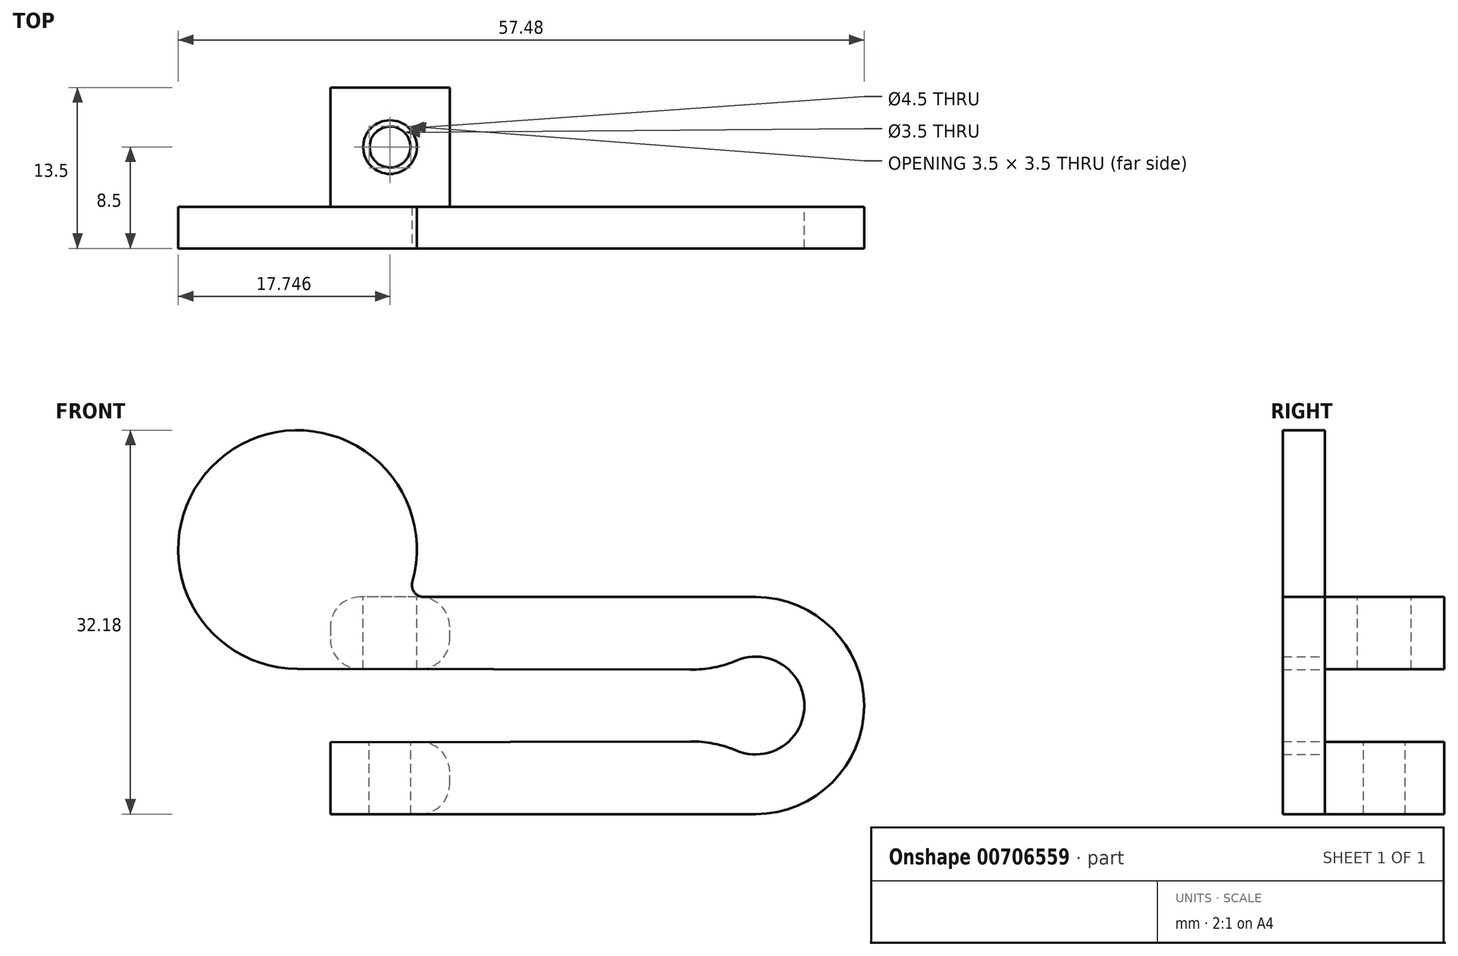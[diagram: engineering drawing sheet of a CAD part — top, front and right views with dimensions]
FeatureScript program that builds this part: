
annotation { "Feature Type Name" : "Feature", "Feature Type Description" : "" }
export const myFeature = defineFeature(function(context is Context, id is Id, definition is map)
    precondition{}
    {
        {
            var Q0;
            Q0=qCreatedBy(makeId("Front.planeOp"),FACE);
            var sketch = newSketch(context, id + "F0", { "sketchPlane" : qUnion([Q0])});
            skArc(sketch, "E0", {"start": v(-2.8, -3) * mm, "mid": v(4.1, 0) * mm, "end": v(-2.8, 3) * mm});
            skArc(sketch, "E1", {"start": v(0, -9.1) * mm, "mid": v(9.1, 0) * mm, "end": v(0, 9.1) * mm});
            skLineSegment(sketch, "E2", {"start": v(0, 9.1) * mm, "end": v(-45, 9.1) * mm});
            skLineSegment(sketch, "E3", {"start": v(0, -9.1) * mm, "end": v(-45, -9.1) * mm});
            skLineSegment(sketch, "E4", {"start": v(-45, 9.1) * mm, "end": v(-45, 3.1) * mm});
            skLineSegment(sketch, "E5", {"start": v(-45, -3.1) * mm, "end": v(-45, -9.1) * mm});
            skLineSegment(sketch, "E6", {"start": v(-45, 3.1) * mm, "end": v(-2.8, 3) * mm});
            skLineSegment(sketch, "E7", {"start": v(-45, -3.1) * mm, "end": v(-2.8, -3) * mm});
            skSolve(sketch);
        }
        {
            var Q0;
            Q0 = qSketchRegion(id + "F0", true);
            extrude(context, id + "F1", {"entities" : qUnion([Q0]), "depth" : 3.5 * mm, "offsetDistance" : 25 * mm});
        }
        {
            var Q0;
            Q0=makeQuery(id+"F1.opExtrude","CAP_FACE",FACE,{"disambiguationData":[OSD([sQuery(id+"F0.wireOp",EDGE,"E0"),sQuery(id+"F0.wireOp",EDGE,"E1"),sQuery(id+"F0.wireOp",EDGE,"E2"),sQuery(id+"F0.wireOp",EDGE,"E3"),sQuery(id+"F0.wireOp",EDGE,"E4"),sQuery(id+"F0.wireOp",EDGE,"E5"),sQuery(id+"F0.wireOp",EDGE,"E6"),sQuery(id+"F0.wireOp",EDGE,"E7")])],"isStart":true});
            var sketch = newSketch(context, id + "F2", { "sketchPlane" : qUnion([Q0])});
            skLineSegment(sketch, "E8", {"start": v(25.63, 9.1) * mm, "end": v(35.63, 9.1) * mm});
            skLineSegment(sketch, "E9", {"start": v(35.63, 9.1) * mm, "end": v(35.63, 3.08) * mm});
            skLineSegment(sketch, "E10", {"start": v(35.63, 3.08) * mm, "end": v(25.63, 3.05) * mm});
            skLineSegment(sketch, "E11", {"start": v(25.63, 3.05) * mm, "end": v(25.63, 9.1) * mm});
            skLineSegment(sketch, "E12", {"start": v(35.63, -3.08) * mm, "end": v(35.63, -9.1) * mm});
            skLineSegment(sketch, "E13", {"start": v(35.63, -9.1) * mm, "end": v(25.63, -9.1) * mm});
            skLineSegment(sketch, "E14", {"start": v(25.63, -9.1) * mm, "end": v(25.63, -3.05) * mm});
            skLineSegment(sketch, "E15", {"start": v(25.63, -3.05) * mm, "end": v(35.63, -3.08) * mm});
            skSolve(sketch);
        }
        {
            var Q0;
            Q0 = qSketchRegion(id + "F2", true);
            extrude(context, id + "F3", {"entities" : qUnion([Q0]), "operationType" : NewBodyOperationType.ADD, "depth" : 10 * mm, "offsetDistance" : 25 * mm});
        }
        {
            var Q0;
            Q0=makeQuery(id+"F3.boolean.opBoolean","MERGE",FACE,{"derivedFrom":[makeQuery(id+"F1.opExtrude","SWEPT_FACE",FACE,{"disambiguationData":[OSD([sQuery(id+"F0.wireOp",EDGE,"E2")])]}),makeQuery(id+"F3.opExtrude","SWEPT_FACE",FACE,{"disambiguationData":[OSD([sQuery(id+"F2.wireOp",EDGE,"pMjsHXQ3-Vv6g-jYmR-rTr3-SYkMuq2vQOZm")])]})]});
            var sketch = newSketch(context, id + "F4", { "sketchPlane" : qUnion([Q0])});
            skCircle(sketch, "E16", {"center": v(-30.63, 5) * mm, "radius": 2.25 * mm});
            skSolve(sketch);
        }
        {
            var Q0;
            Q0 = qSketchRegion(id + "F4", true);
            extrude(context, id + "F5", {"entities" : qUnion([Q0]), "operationType" : NewBodyOperationType.REMOVE, "oppositeDirection" : true, "depth" : 10 * mm, "offsetDistance" : 25 * mm});
        }
        {
            var Q0;
            Q0=makeQuery(id+"F3.boolean.opBoolean","MERGE",FACE,{"derivedFrom":[makeQuery(id+"F1.opExtrude","SWEPT_FACE",FACE,{"disambiguationData":[OSD([sQuery(id+"F0.wireOp",EDGE,"E2")])]}),makeQuery(id+"F3.opExtrude","SWEPT_FACE",FACE,{"disambiguationData":[OSD([sQuery(id+"F2.wireOp",EDGE,"pMjsHXQ3-Vv6g-jYmR-rTr3-SYkMuq2vQOZm")])]})]});
            var sketch = newSketch(context, id + "F6", { "sketchPlane" : qUnion([Q0])});
            skCircle(sketch, "E17", {"center": v(-30.63, 5) * mm, "radius": 1.75 * mm});
            skSolve(sketch);
        }
        {
            var Q0;
            Q0 = qSketchRegion(id + "F6", true);
            extrude(context, id + "F7", {"entities" : qUnion([Q0]), "operationType" : NewBodyOperationType.REMOVE, "oppositeDirection" : true, "depth" : 25 * mm, "offsetDistance" : 25 * mm});
        }
        {
            var Q0;
            Q0=makeQuery(id+"F1.opExtrude","CAP_FACE",FACE,{"disambiguationData":[OSD([sQuery(id+"F0.wireOp",EDGE,"E0"),sQuery(id+"F0.wireOp",EDGE,"E1"),sQuery(id+"F0.wireOp",EDGE,"E2"),sQuery(id+"F0.wireOp",EDGE,"E3"),sQuery(id+"F0.wireOp",EDGE,"E4"),sQuery(id+"F0.wireOp",EDGE,"E5"),sQuery(id+"F0.wireOp",EDGE,"E6"),sQuery(id+"F0.wireOp",EDGE,"E7")])],"isStart":false});
            var sketch = newSketch(context, id + "F8", { "sketchPlane" : qUnion([Q0])});
            skCircle(sketch, "E18", {"center": v(-38.38, 13.08) * mm, "radius": 10 * mm});
            skSolve(sketch);
        }
        {
            var Q0;
            Q0 = qSketchRegion(id + "F8", true);
            var Q1;
            Q1=makeQuery(id+"F1.opExtrude","CAP_FACE",FACE,{"disambiguationData":[OSD([sQuery(id+"F0.wireOp",EDGE,"E0"),sQuery(id+"F0.wireOp",EDGE,"E1"),sQuery(id+"F0.wireOp",EDGE,"E2"),sQuery(id+"F0.wireOp",EDGE,"E3"),sQuery(id+"F0.wireOp",EDGE,"E4"),sQuery(id+"F0.wireOp",EDGE,"E5"),sQuery(id+"F0.wireOp",EDGE,"E6"),sQuery(id+"F0.wireOp",EDGE,"E7")])],"isStart":true});
            extrude(context, id + "F9", {"entities" : qUnion([Q0]), "operationType" : NewBodyOperationType.ADD, "endBound" : BoundingType.UP_TO_SURFACE, "oppositeDirection" : true, "depth" : 25 * mm, "endBoundEntityFace" : qUnion([Q1]), "offsetDistance" : 25 * mm});
        }
        {
            var Q0;
            Q0=makeQuery(id+"F3.boolean.opBoolean","MERGE",EDGE,{"derivedFrom":[makeQuery(id+"F1.opExtrude","SWEPT_EDGE",EDGE,{"disambiguationData":[OSD([sQuery(id+"F0.wireOp",EDGE,"E4"),sQuery(id+"F0.wireOp",EDGE,"E6")])]}),makeQuery(id+"F3.opExtrude","SWEPT_EDGE",EDGE,{"disambiguationData":[OSD([sQuery(id+"F2.wireOp",EDGE,"VnQjhJev-6pRI-Fd25-12oq-4aVABt8pIq3j"),sQuery(id+"F2.wireOp",EDGE,"sn0lMUrj-LP6i-RNEb-L6wM-ymogfDIRcxsj")])]})]});
            var Q1;
            Q1=makeQuery(id+"F3.boolean.opBoolean","MERGE",EDGE,{"derivedFrom":[makeQuery(id+"F1.opExtrude","SWEPT_EDGE",EDGE,{"disambiguationData":[OSD([sQuery(id+"F0.wireOp",EDGE,"E2"),sQuery(id+"F0.wireOp",EDGE,"E4")])]}),makeQuery(id+"F3.opExtrude","SWEPT_EDGE",EDGE,{"disambiguationData":[OSD([sQuery(id+"F2.wireOp",EDGE,"pMjsHXQ3-Vv6g-jYmR-rTr3-SYkMuq2vQOZm"),sQuery(id+"F2.wireOp",EDGE,"VnQjhJev-6pRI-Fd25-12oq-4aVABt8pIq3j")])]})]});
            fillet(context, id + "F10", {"entities" : qUnion([Q0, Q1]), "radius" : 3 * mm, "tangentPropagation" : true, "allowEdgeOverflow" : false});
        }
        {
            var Q0;
            Q0=makeQuery(id+"F1.opExtrude","SWEPT_EDGE",EDGE,{"disambiguationData":[OSD([sQuery(id+"F0.wireOp",EDGE,"E0"),sQuery(id+"F0.wireOp",EDGE,"E7")])]});
            var Q1;
            Q1=makeQuery(id+"F1.opExtrude","SWEPT_EDGE",EDGE,{"disambiguationData":[OSD([sQuery(id+"F0.wireOp",EDGE,"E0"),sQuery(id+"F0.wireOp",EDGE,"E6")])]});
            fillet(context, id + "F11", {"entities" : qUnion([Q0, Q1]), "radius" : 10 * mm, "tangentPropagation" : true, "allowEdgeOverflow" : false});
        }
        {
            var Q0;
            Q0=makeQuery(id+"F10.opFillet","BLEND_EDGE",EDGE,{"blendedFrom":[makeQuery(id+"F1.opExtrude","SWEPT_EDGE",EDGE,{"disambiguationData":[OSD([sQuery(id+"F0.wireOp",EDGE,"E4"),sQuery(id+"F0.wireOp",EDGE,"E6")])]}),makeQuery(id+"F9.opExtrude","SWEPT_FACE",FACE,{"disambiguationData":[OSD([sQuery(id+"F8.wireOp",EDGE,"E18")])]})],"blendedInto":[makeQuery(id+"F9.opExtrude","SWEPT_FACE",FACE,{"disambiguationData":[OSD([sQuery(id+"F8.wireOp",EDGE,"E18")])]})]});
            fillet(context, id + "F12", {"entities" : qUnion([Q0]), "radius" : 5 * mm, "tangentPropagation" : true, "allowEdgeOverflow" : false});
        }
        {
            var Q0;
            Q0=makeQuery(id+"F9.boolean.opBoolean","INTERSECT",EDGE,{"derivedFrom":[makeQuery(id+"F3.boolean.opBoolean","MERGE",FACE,{"derivedFrom":[makeQuery(id+"F1.opExtrude","SWEPT_FACE",FACE,{"disambiguationData":[OSD([sQuery(id+"F0.wireOp",EDGE,"E2")])]}),makeQuery(id+"F3.opExtrude","SWEPT_FACE",FACE,{"disambiguationData":[OSD([sQuery(id+"F2.wireOp",EDGE,"E8")])]})]}),makeQuery(id+"F9.opExtrude","SWEPT_FACE",FACE,{"disambiguationData":[OSD([sQuery(id+"F8.wireOp",EDGE,"E18")])]})]});
            fillet(context, id + "F13", {"entities" : qUnion([Q0]), "radius" : 1 * mm, "tangentPropagation" : true, "allowEdgeOverflow" : false});
        }
        {
            var Q0;
            {var subQ0=sQuery(id+"F0.wireOp",EDGE,"E5");var subQ1=sQuery(id+"F0.wireOp",EDGE,"E7");var subQ2=sQuery(id+"F0.wireOp",EDGE,"E3");Q0=makeQuery(id+"F3.boolean.opBoolean","SPLIT",FACE,{"disambiguationData":[TD([makeQuery(id+"F1.opExtrude","SWEPT_FACE",FACE,{"disambiguationData":[OSD([subQ0])]})])],"derivedFrom":makeQuery(id+"F1.opExtrude","CAP_FACE",FACE,{"disambiguationData":[OSD([sQuery(id+"F0.wireOp",EDGE,"E0"),sQuery(id+"F0.wireOp",EDGE,"E1"),sQuery(id+"F0.wireOp",EDGE,"E2"),subQ2,sQuery(id+"F0.wireOp",EDGE,"E4"),subQ0,sQuery(id+"F0.wireOp",EDGE,"E6"),subQ1])],"isStart":true})});}
            var sketch = newSketch(context, id + "F14", { "sketchPlane" : qUnion([Q0])});
            skLineSegment(sketch, "E19", {"start": v(35.63, -3.08) * mm, "end": v(45, -3.1) * mm});
            skLineSegment(sketch, "E20", {"start": v(45, -3.1) * mm, "end": v(45, -9.1) * mm});
            skLineSegment(sketch, "E21", {"start": v(45, -9.1) * mm, "end": v(35.63, -9.1) * mm});
            skLineSegment(sketch, "E22", {"start": v(35.63, -9.1) * mm, "end": v(35.63, -3.08) * mm});
            skSolve(sketch);
        }
        {
            var Q0;
            Q0 = qSketchRegion(id + "F14", true);
            extrude(context, id + "F15", {"entities" : qUnion([Q0]), "operationType" : NewBodyOperationType.REMOVE, "oppositeDirection" : true, "depth" : 25 * mm, "offsetDistance" : 25 * mm});
        }
        {
            var Q0;
            Q0=makeQuery(id+"F15.boolean.opBoolean","MERGE",EDGE,{"derivedFrom":[makeQuery(id+"F3.opExtrude","SWEPT_EDGE",EDGE,{"disambiguationData":[OSD([sQuery(id+"F0.wireOp",EDGE,"E7"),sQuery(id+"F2.wireOp",EDGE,"E12"),sQuery(id+"F2.wireOp",EDGE,"E15")])]}),makeQuery(id+"F15.opExtrude","SWEPT_EDGE",EDGE,{"disambiguationData":[OSD([sQuery(id+"F14.wireOp",EDGE,"E19"),sQuery(id+"F14.wireOp",EDGE,"E22")])]})]});
            var Q1;
            Q1=makeQuery(id+"F15.boolean.opBoolean","MERGE",EDGE,{"derivedFrom":[makeQuery(id+"F3.opExtrude","SWEPT_EDGE",EDGE,{"disambiguationData":[OSD([sQuery(id+"F0.wireOp",EDGE,"E3"),sQuery(id+"F2.wireOp",EDGE,"E12"),sQuery(id+"F2.wireOp",EDGE,"E13")])]}),makeQuery(id+"F15.opExtrude","SWEPT_EDGE",EDGE,{"disambiguationData":[OSD([sQuery(id+"F14.wireOp",EDGE,"E21"),sQuery(id+"F14.wireOp",EDGE,"E22")])]})]});
            var Q2;
            Q2=makeQuery(id+"F3.opExtrude","SWEPT_EDGE",EDGE,{"disambiguationData":[OSD([sQuery(id+"F0.wireOp",EDGE,"E7"),sQuery(id+"F2.wireOp",EDGE,"E14"),sQuery(id+"F2.wireOp",EDGE,"E15")])]});
            var Q3;
            Q3=makeQuery(id+"F3.opExtrude","SWEPT_EDGE",EDGE,{"disambiguationData":[OSD([sQuery(id+"F0.wireOp",EDGE,"E3"),sQuery(id+"F2.wireOp",EDGE,"E13"),sQuery(id+"F2.wireOp",EDGE,"E14")])]});
            var Q4;
            Q4=makeQuery(id+"F3.opExtrude","SWEPT_EDGE",EDGE,{"disambiguationData":[OSD([sQuery(id+"F0.wireOp",EDGE,"E2"),sQuery(id+"F2.wireOp",EDGE,"E8"),sQuery(id+"F2.wireOp",EDGE,"E11")])]});
            var Q5;
            Q5=makeQuery(id+"F3.opExtrude","SWEPT_EDGE",EDGE,{"disambiguationData":[OSD([sQuery(id+"F0.wireOp",EDGE,"E6"),sQuery(id+"F2.wireOp",EDGE,"E10"),sQuery(id+"F2.wireOp",EDGE,"E11")])]});
            var Q6;
            Q6=makeQuery(id+"F13.opFillet","BLEND_EDGE",EDGE,{"blendedFrom":[makeQuery(id+"F9.boolean.opBoolean","INTERSECT",EDGE,{"derivedFrom":[makeQuery(id+"F3.boolean.opBoolean","MERGE",FACE,{"derivedFrom":[makeQuery(id+"F1.opExtrude","SWEPT_FACE",FACE,{"disambiguationData":[OSD([sQuery(id+"F0.wireOp",EDGE,"E2")])]}),makeQuery(id+"F3.opExtrude","SWEPT_FACE",FACE,{"disambiguationData":[OSD([sQuery(id+"F2.wireOp",EDGE,"E8")])]})]}),makeQuery(id+"F9.opExtrude","SWEPT_FACE",FACE,{"disambiguationData":[OSD([sQuery(id+"F8.wireOp",EDGE,"E18")])]})]}),makeQuery(id+"F3.opExtrude","SWEPT_FACE",FACE,{"disambiguationData":[OSD([sQuery(id+"F2.wireOp",EDGE,"E9")])]})],"blendedInto":[makeQuery(id+"F3.opExtrude","SWEPT_FACE",FACE,{"disambiguationData":[OSD([sQuery(id+"F2.wireOp",EDGE,"E9")])]})]});
            var Q7;
            Q7=makeQuery(id+"F3.opExtrude","SWEPT_EDGE",EDGE,{"disambiguationData":[OSD([sQuery(id+"F0.wireOp",EDGE,"E6"),sQuery(id+"F2.wireOp",EDGE,"E9"),sQuery(id+"F2.wireOp",EDGE,"E10")])]});
            fillet(context, id + "F16", {"entities" : qUnion([Q0, Q1, Q2, Q3, Q4, Q5, Q6, Q7]), "radius" : 2.5 * mm, "tangentPropagation" : true, "allowEdgeOverflow" : false});
        }
        {
            var Q0;
            Q0=makeQuery(id+"F3.opExtrude","SWEPT_EDGE",EDGE,{"disambiguationData":[OSD([sQuery(id+"F0.wireOp",EDGE,"E2"),sQuery(id+"F2.wireOp",EDGE,"E8"),sQuery(id+"F2.wireOp",EDGE,"E9")])]});
            fillet(context, id + "F17", {"entities" : qUnion([Q0]), "radius" : 2.5 * mm, "tangentPropagation" : true, "allowEdgeOverflow" : false});
        }
        {
            var Q0;
            {var subQ0=sQuery(id+"F0.wireOp",EDGE,"E6");var subQ1=sQuery(id+"F0.wireOp",EDGE,"E4");var subQ2=sQuery(id+"F0.wireOp",EDGE,"E2");Q0=makeQuery(id+"F9.boolean.opBoolean","MERGE",FACE,{"derivedFrom":[makeQuery(id+"F3.boolean.opBoolean","SPLIT",FACE,{"disambiguationData":[TD([makeQuery(id+"F1.opExtrude","SWEPT_FACE",FACE,{"disambiguationData":[OSD([subQ1])]})])],"derivedFrom":makeQuery(id+"F1.opExtrude","CAP_FACE",FACE,{"disambiguationData":[OSD([sQuery(id+"F0.wireOp",EDGE,"E0"),sQuery(id+"F0.wireOp",EDGE,"E1"),subQ2,sQuery(id+"F0.wireOp",EDGE,"E3"),subQ1,sQuery(id+"F0.wireOp",EDGE,"E5"),subQ0,sQuery(id+"F0.wireOp",EDGE,"E7")])],"isStart":true})}),makeQuery(id+"F9.opExtrude","CAP_FACE",FACE,{"disambiguationData":[OSD([sQuery(id+"F8.wireOp",EDGE,"E18")])],"isStart":false})]});}
            var sketch = newSketch(context, id + "F18", { "sketchPlane" : qUnion([Q0])});
            skPoint(sketch, "E23.first.point", {"position": v(31.92, 20.71) * mm});
            skPoint(sketch, "E23.second.point", {"position": v(46.93, 18.27) * mm});
            skPoint(sketch, "E23.third.point", {"position": v(46.44, 7.16) * mm});
            skLineSegment(sketch, "E24", {"start": v(45.7, 6.27) * mm, "end": v(47.25, 3.38) * mm});
            skLineSegment(sketch, "E25", {"start": v(47.25, 3.38) * mm, "end": v(40.26, 1.66) * mm});
            skLineSegment(sketch, "E26", {"start": v(40.26, 1.66) * mm, "end": v(38.4, 3.08) * mm});
            skArc(sketch, "E27.trimOffspring", {"start": v(38.4, 3.08) * mm, "mid": v(42.39, 3.92) * mm, "end": v(45.7, 6.27) * mm});
            skSolve(sketch);
        }
        {
            var Q0;
            Q0 = qSketchRegion(id + "F18", true);
            extrude(context, id + "F19", {"entities" : qUnion([Q0]), "operationType" : NewBodyOperationType.REMOVE, "oppositeDirection" : true, "depth" : 25 * mm, "offsetDistance" : 25 * mm});
        }
    });
